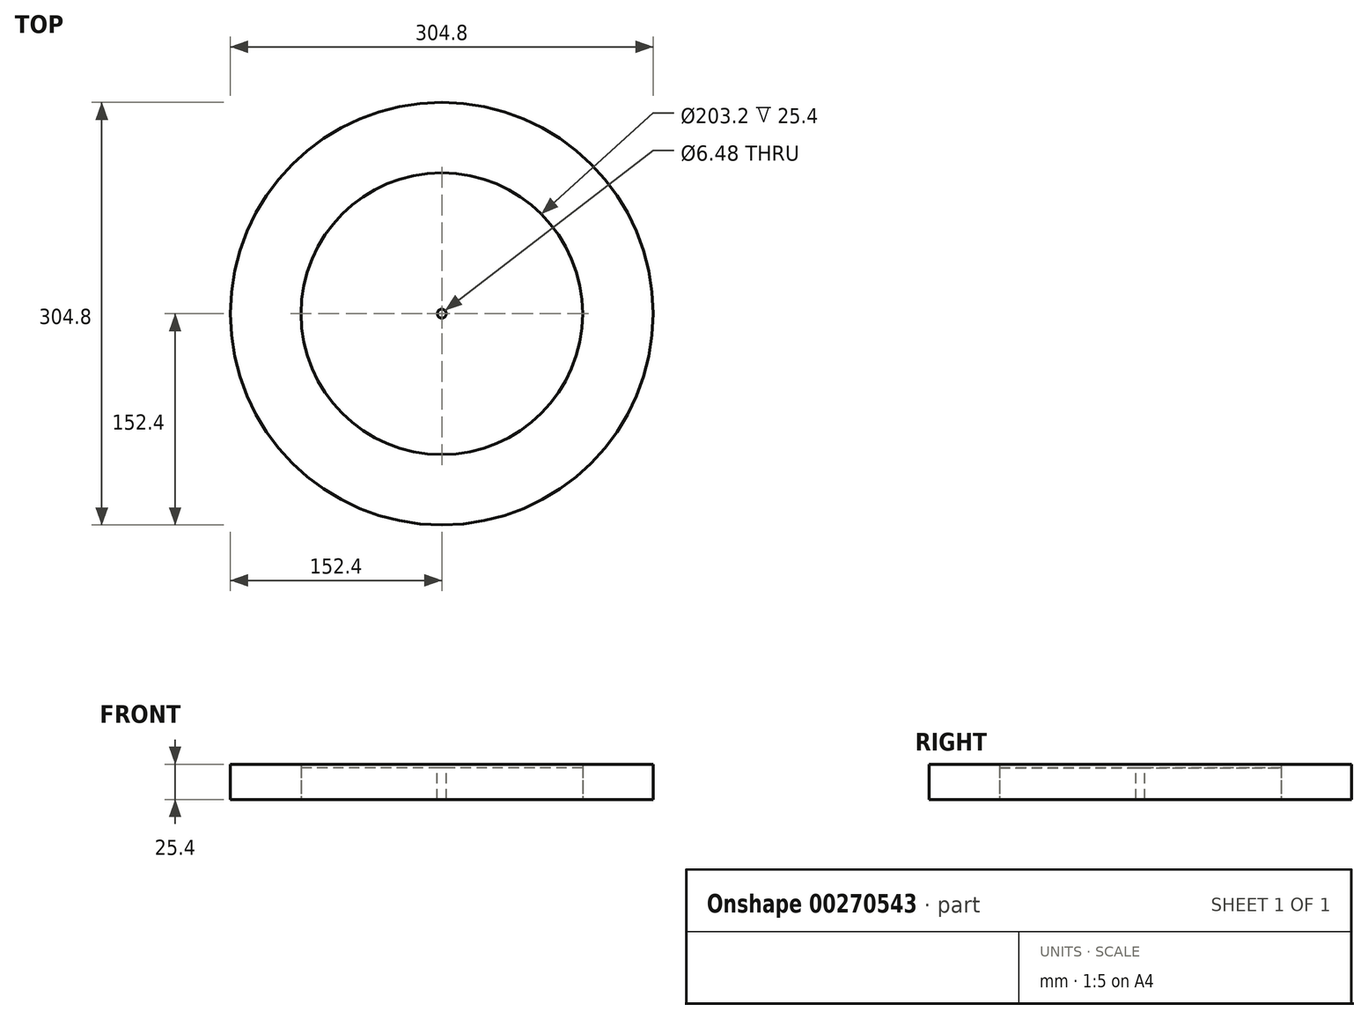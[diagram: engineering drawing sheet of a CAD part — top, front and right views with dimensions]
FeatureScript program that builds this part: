
annotation { "Feature Type Name" : "Feature", "Feature Type Description" : "" }
export const myFeature = defineFeature(function(context is Context, id is Id, definition is map)
    precondition{}
    {
        {
            var Q0;
            Q0=qCreatedBy(makeId("Top.planeOp"),FACE);
            var sketch = newSketch(context, id + "F0", { "sketchPlane" : qUnion([Q0])});
            skCircle(sketch, "E0", {"center": v(0, 0) * mm, "radius": 101.6 * mm});
            skSolve(sketch);
        }
        {
            var Q0;
            Q0=makeQuery(id+"F0.imprint","IMPRINT",FACE,{"disambiguationData":[TD([[makeQuery(id+"F0.imprint","IMPRINT",EDGE,{"derivedFrom":sQuery(id+"F0.wireOp",EDGE,"E0")}),1.0]])]});
            extrude(context, id + "F1", {"entities" : qUnion([Q0]), "depth" : 22.86 * mm});
        }
        {
            var Q0;
            Q0=makeQuery(id+"F1.opExtrude","CAP_FACE",FACE,{"disambiguationData":[OSD([sQuery(id+"F0.wireOp",EDGE,"E0")])],"isStart":false});
            var sketch = newSketch(context, id + "F2", { "sketchPlane" : qUnion([Q0])});
            skCircle(sketch, "E1", {"center": v(0, 0) * mm, "radius": 3.24 * mm});
            skSolve(sketch);
        }
        {
            var Q0;
            Q0=makeQuery(id+"F2.imprint","IMPRINT",FACE,{"disambiguationData":[TD([[makeQuery(id+"F2.imprint","IMPRINT",EDGE,{"derivedFrom":sQuery(id+"F2.wireOp",EDGE,"E1")}),1.0]])]});
            var Q1;
            Q1=makeQuery(id+"F1.opExtrude","CAP_FACE",FACE,{"disambiguationData":[OSD([sQuery(id+"F0.wireOp",EDGE,"E0")])],"isStart":true});
            extrude(context, id + "F3", {"entities" : qUnion([Q0]), "operationType" : NewBodyOperationType.REMOVE, "endBound" : BoundingType.UP_TO_SURFACE, "oppositeDirection" : true, "endBoundEntityFace" : qUnion([Q1]), "depth" : 25.4 * mm});
        }
        {
            var Q0;
            Q0=qCreatedBy(makeId("Top.planeOp"),FACE);
            var sketch = newSketch(context, id + "F4", { "sketchPlane" : qUnion([Q0])});
            skCircle(sketch, "E2", {"center": v(0, 0) * mm, "radius": 152.4 * mm});
            skCircle(sketch, "E3", {"center": v(0, 0) * mm, "radius": 101.6 * mm});
            skSolve(sketch);
        }
        {
            var Q0;
            Q0=makeQuery(id+"F4.imprint","IMPRINT",FACE,{"disambiguationData":[TD([[makeQuery(id+"F4.imprint","IMPRINT",EDGE,{"derivedFrom":sQuery(id+"F4.wireOp",EDGE,"E2")}),1.0]])]});
            extrude(context, id + "F5", {"entities" : qUnion([Q0]), "depth" : 25.4 * mm});
        }
    });
